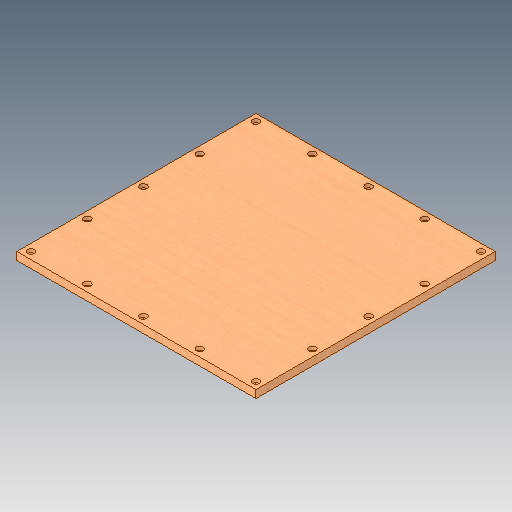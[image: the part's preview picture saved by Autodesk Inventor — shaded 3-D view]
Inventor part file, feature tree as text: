
AUTODESK INVENTOR PART (.ipt)
format: ipt  version: 2018.2 (Build 222227000, 227)  size: 218,624 bytes
history: native  units: mm
features: sketch x2, extrude x1, hole x1, pattern_linear x1, pattern_circular x1, projected_geometry x1
ambient origin geometry x8: Origin, YZ Plane, XZ Plane, XY Plane, X Axis, Y Axis, Z Axis, Center Point
bodies: Solid1 (feature_tree)
feature tree (7):
  extrude  "Extrusion1"  Depth=340.0mm
  hole  "Hole1"  [1 undecoded]
  pattern_linear  "Rectangular Pattern1"  Spacing1=10.0mm  [1 undecoded]
  pattern_circular  "Circular Pattern1"  [2 undecoded]
  sketch  "Sketch1"  dims[d0=340.0mm d1=340.0mm]
  sketch  "Sketch2"  dims[d2=11.1125mm d3=0.0mm d4=10.0mm d5=10.0mm d6=5.5mm d7=6.0mm d8=10.0mm d9=5.0mm d10=90.0deg d11=8.0mm d12=20.594885mm d13=20.0mm d15=320.0mm d16=50.0mm d18=80.0mm d19=20.0mm d20=90.0deg]
  projected_geometry  "Projected Loop1"
note: 4 required parameter values undecoded (feature->parameter linkage not recoverable at this tier; creation-order binding heuristic only, values carry confidence <= 0.55)
